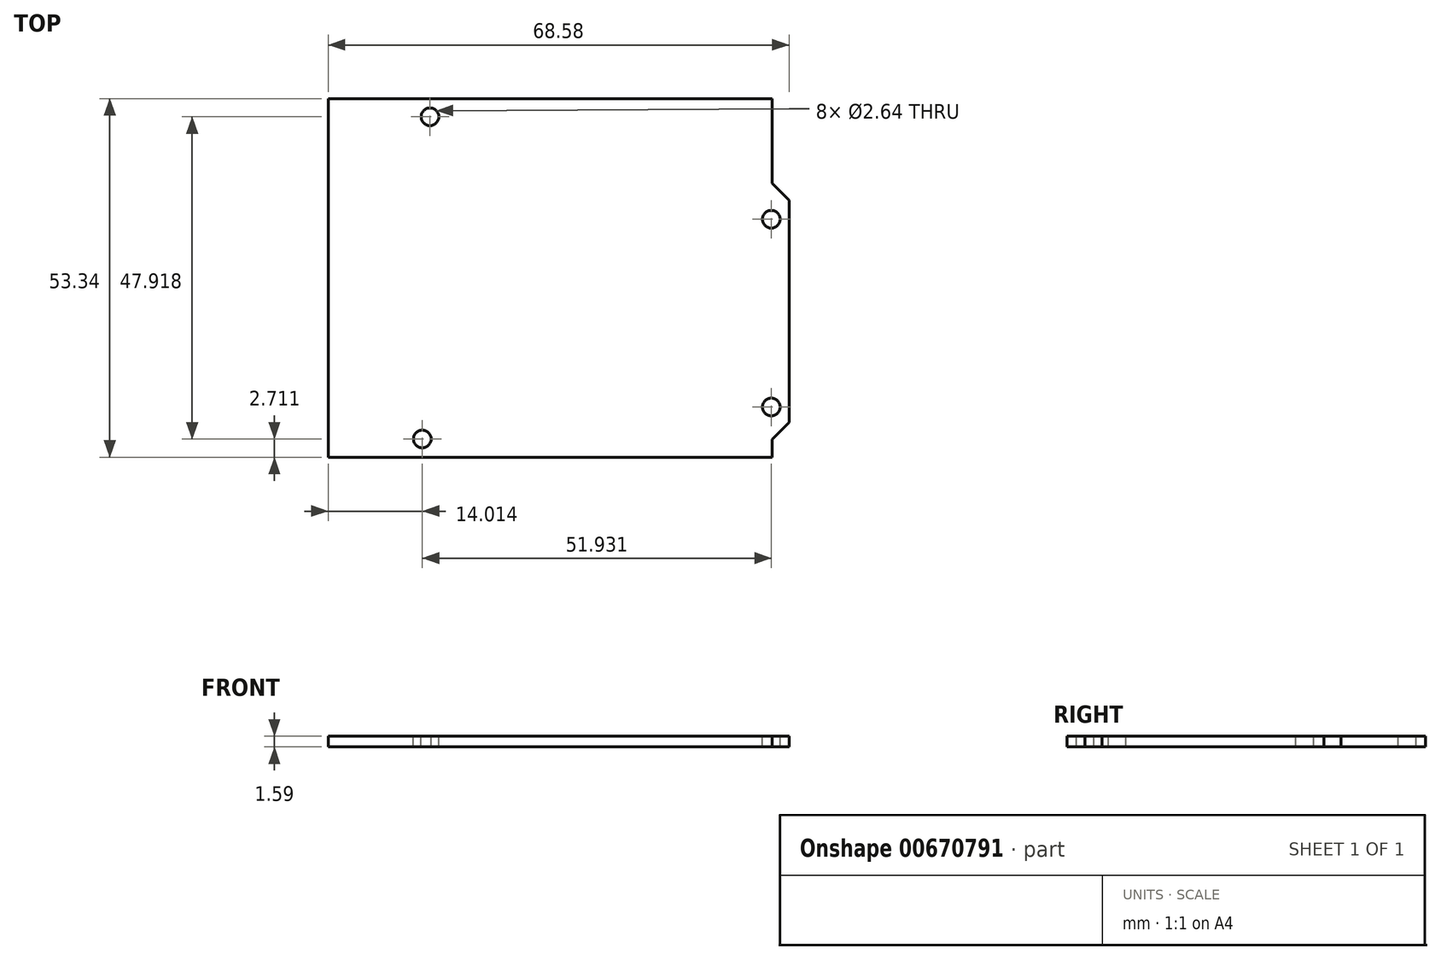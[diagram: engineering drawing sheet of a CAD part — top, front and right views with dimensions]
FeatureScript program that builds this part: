
annotation { "Feature Type Name" : "Feature", "Feature Type Description" : "" }
export const myFeature = defineFeature(function(context is Context, id is Id, definition is map)
    precondition{}
    {
        {
            var Q0;
            Q0=qCreatedBy(makeId("Top.planeOp"),FACE);
            var sketch = newSketch(context, id + "F0", { "sketchPlane" : qUnion([Q0])});
            skLineSegment(sketch, "E0.bottom", {"start": v(-33.02, -26.67) * mm, "end": v(33.02, -26.67) * mm});
            skLineSegment(sketch, "E0.top", {"start": v(-33.02, 26.67) * mm, "end": v(33.02, 26.67) * mm});
            skLineSegment(sketch, "E0.left", {"start": v(-33.02, -26.67) * mm, "end": v(-33.02, 26.67) * mm});
            skLineSegment(sketch, "E0.right", {"start": v(33.02, -26.67) * mm, "end": v(33.02, 26.67) * mm});
            skLineSegment(sketch, "E1", {"start": v(0, 0) * mm, "end": v(-33.02, 0) * mm, "construction": true});
            skLineSegment(sketch, "E2", {"start": v(0, 0) * mm, "end": v(0, 26.67) * mm, "construction": true});
            skLineSegment(sketch, "E3", {"start": v(33.02, -24) * mm, "end": v(35.56, -21.46) * mm});
            skLineSegment(sketch, "E4", {"start": v(35.56, -21.46) * mm, "end": v(35.56, 11.56) * mm});
            skLineSegment(sketch, "E5", {"start": v(35.56, 11.56) * mm, "end": v(33.02, 14.1) * mm});
            skSolve(sketch);
        }
        {
            var Q0;
            Q0 = qSketchRegion(id + "F0", true);
            extrude(context, id + "F1", {"entities" : qUnion([Q0]), "depth" : 1.59 * mm, "offsetDistance" : 25 * mm});
        }
        {
            var Q0;
            Q0=makeQuery(id+"F1.opExtrude","CAP_FACE",FACE,{"disambiguationData":[OSD([sQuery(id+"F0.wireOp",EDGE,"E0.bottom"),sQuery(id+"F0.wireOp",EDGE,"E0.top"),sQuery(id+"F0.wireOp",EDGE,"E0.left"),sQuery(id+"F0.wireOp",EDGE,"E0.right"),sQuery(id+"F0.wireOp",EDGE,"E3"),sQuery(id+"F0.wireOp",EDGE,"E4"),sQuery(id+"F0.wireOp",EDGE,"E5")])],"isStart":false});
            var sketch = newSketch(context, id + "F2", { "sketchPlane" : qUnion([Q0])});
            skCircle(sketch, "E6", {"center": v(32.93, -19.2) * mm, "radius": 1.32 * mm});
            skCircle(sketch, "E7", {"center": v(32.93, 8.72) * mm, "radius": 1.32 * mm});
            skCircle(sketch, "E8", {"center": v(-19, -23.96) * mm, "radius": 1.32 * mm});
            skCircle(sketch, "E9", {"center": v(-17.86, 23.96) * mm, "radius": 1.32 * mm});
            skSolve(sketch);
        }
        {
            var Q0;
            Q0 = qSketchRegion(id + "F2", true);
            extrude(context, id + "F3", {"entities" : qUnion([Q0]), "operationType" : NewBodyOperationType.REMOVE, "endBound" : BoundingType.THROUGH_ALL, "oppositeDirection" : true, "depth" : 25 * mm, "offsetDistance" : 25 * mm});
        }
    });
